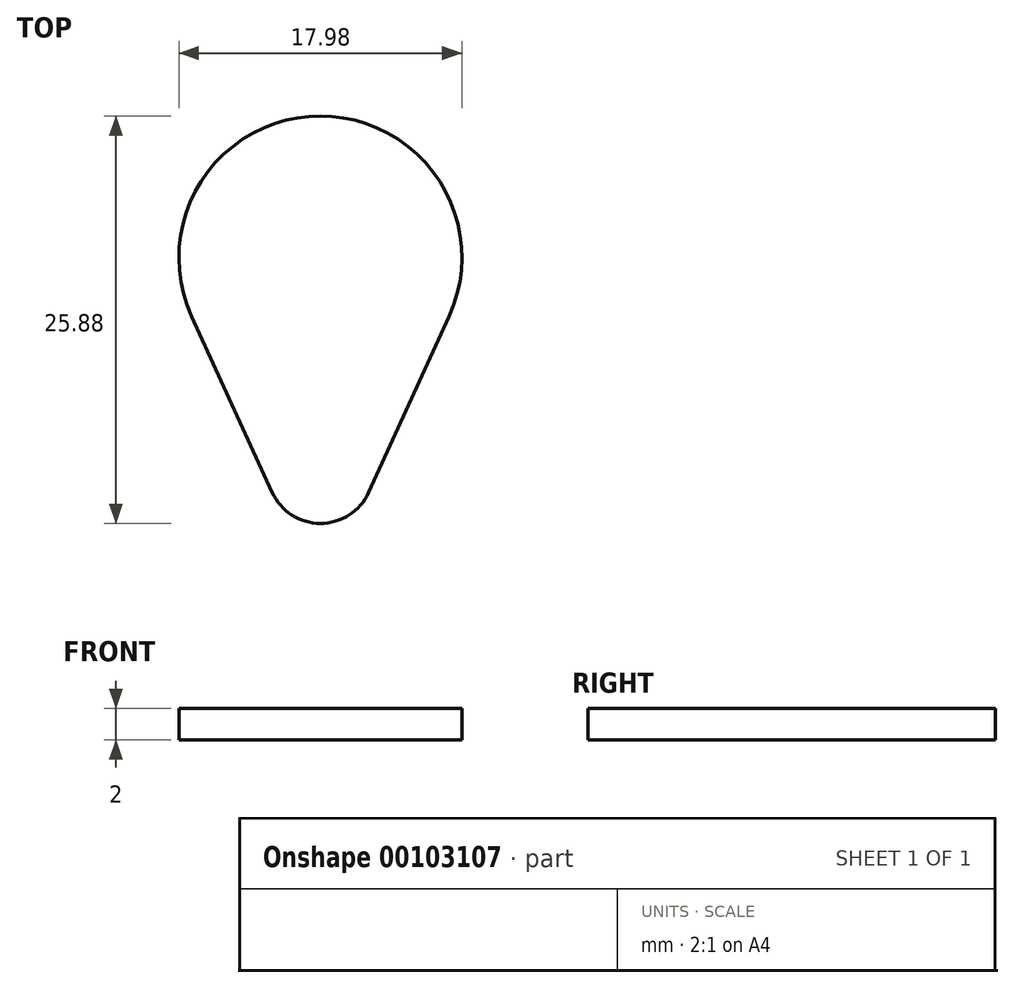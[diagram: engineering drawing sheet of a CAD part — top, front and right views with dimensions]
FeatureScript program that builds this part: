
annotation { "Feature Type Name" : "Feature", "Feature Type Description" : "" }
export const myFeature = defineFeature(function(context is Context, id is Id, definition is map)
    precondition{}
    {
        {
            var Q0;
            Q0=qCreatedBy(makeId("Top.planeOp"),FACE);
            var sketch = newSketch(context, id + "F0", { "sketchPlane" : qUnion([Q0])});
            skLineSegment(sketch, "E0", {"start": v(-3.07, -8.68) * mm, "end": v(-8.18, 2.5) * mm});
            skLineSegment(sketch, "E1.MirrorCS", {"start": v(3.07, -8.68) * mm, "end": v(8.18, 2.5) * mm});
            skArc(sketch, "E2", {"start": v(-3.07, -8.68) * mm, "mid": v(0, -10.65) * mm, "end": v(3.07, -8.68) * mm});
            skArc(sketch, "E3", {"start": v(8.18, 2.5) * mm, "mid": v(0, 15.23) * mm, "end": v(-8.18, 2.5) * mm});
            skSolve(sketch);
        }
        {
            var Q0;
            Q0=makeQuery(id+"F0.imprint","IMPRINT",FACE,{"disambiguationData":[TD([[makeQuery(id+"F0.imprint","IMPRINT",EDGE,{"derivedFrom":sQuery(id+"F0.wireOp",EDGE,"E0")}),-1.0]])]});
            extrude(context, id + "F1", {"entities" : qUnion([Q0]), "depth" : 2 * mm});
        }
    });
